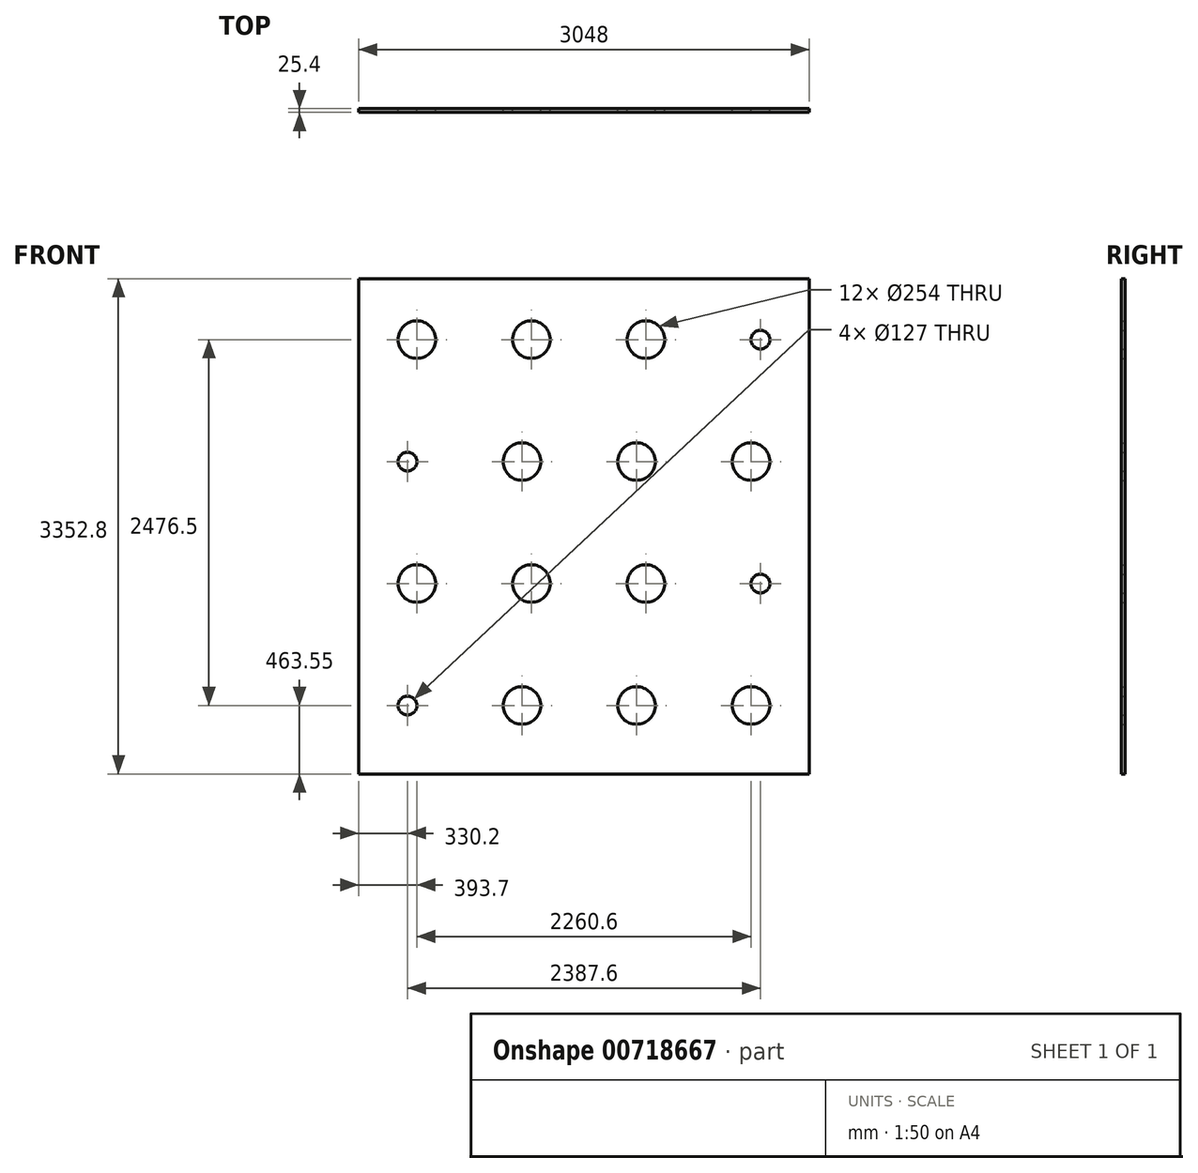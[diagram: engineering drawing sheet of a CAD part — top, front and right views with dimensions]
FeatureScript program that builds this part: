
annotation { "Feature Type Name" : "Feature", "Feature Type Description" : "" }
export const myFeature = defineFeature(function(context is Context, id is Id, definition is map)
    precondition{}
    {
        {
            var Q0;
            Q0=qCreatedBy(makeId("Front.planeOp"),FACE);
            var sketch = newSketch(context, id + "F0", { "sketchPlane" : qUnion([Q0])});
            skLineSegment(sketch, "E0", {"start": v(0, 0) * mm, "end": v(0, 3352.8) * mm});
            skLineSegment(sketch, "E1", {"start": v(0, 3352.8) * mm, "end": v(3048, 3352.8) * mm});
            skLineSegment(sketch, "E2", {"start": v(3048, 3352.8) * mm, "end": v(3048, 0) * mm});
            skLineSegment(sketch, "E3", {"start": v(3048, 0) * mm, "end": v(0, 0) * mm});
            skCircle(sketch, "E4", {"center": v(393.7, 2940.05) * mm, "radius": 127 * mm});
            skCircle(sketch, "E5", {"center": v(1168.4, 2940.05) * mm, "radius": 127 * mm});
            skCircle(sketch, "E6", {"center": v(1943.1, 2940.05) * mm, "radius": 127 * mm});
            skCircle(sketch, "E7", {"center": v(2717.8, 2940.05) * mm, "radius": 63.5 * mm});
            skCircle(sketch, "E8", {"center": v(2654.3, 2114.55) * mm, "radius": 127 * mm});
            skCircle(sketch, "E9", {"center": v(1879.6, 2114.55) * mm, "radius": 127 * mm});
            skCircle(sketch, "E10", {"center": v(1104.9, 2114.55) * mm, "radius": 127 * mm});
            skCircle(sketch, "E11", {"center": v(330.2, 2114.55) * mm, "radius": 63.5 * mm});
            skCircle(sketch, "E12", {"center": v(393.7, 1289.05) * mm, "radius": 127 * mm});
            skCircle(sketch, "E13", {"center": v(1168.4, 1289.05) * mm, "radius": 127 * mm});
            skCircle(sketch, "E14", {"center": v(1943.1, 1289.05) * mm, "radius": 127 * mm});
            skCircle(sketch, "E15", {"center": v(2717.8, 1289.05) * mm, "radius": 63.5 * mm});
            skCircle(sketch, "E16", {"center": v(2654.3, 463.55) * mm, "radius": 127 * mm});
            skCircle(sketch, "E17", {"center": v(1879.6, 463.55) * mm, "radius": 127 * mm});
            skCircle(sketch, "E18", {"center": v(1104.9, 463.55) * mm, "radius": 127 * mm});
            skCircle(sketch, "E19", {"center": v(330.2, 463.55) * mm, "radius": 63.5 * mm});
            skPoint(sketch, "E20", {"position": v(1524, 3352.8) * mm});
            skSolve(sketch);
        }
        {
            var Q0;
            Q0=makeQuery(id+"F0.imprint","IMPRINT",FACE,{"disambiguationData":[TD([[makeQuery(id+"F0.imprint","IMPRINT",EDGE,{"derivedFrom":sQuery(id+"F0.wireOp",EDGE,"E0")}),-1.0]])]});
            extrude(context, id + "F1", {"entities" : qUnion([Q0]), "depth" : 25.4 * mm, "offsetDistance" : 25.4 * mm});
        }
    });
